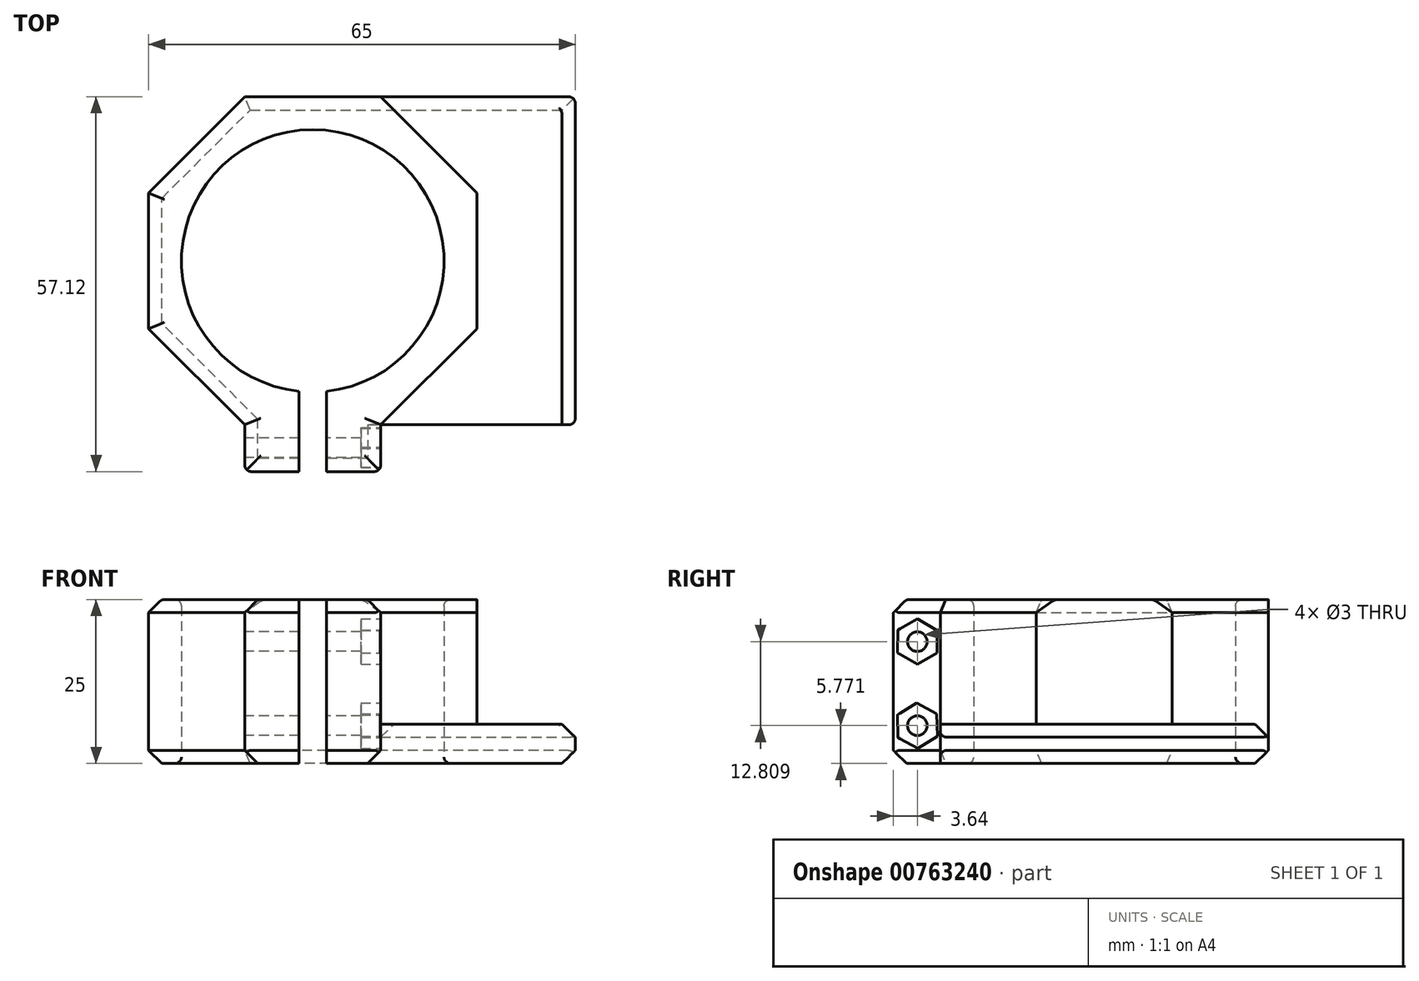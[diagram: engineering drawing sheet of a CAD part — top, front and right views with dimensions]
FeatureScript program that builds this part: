
annotation { "Feature Type Name" : "Feature", "Feature Type Description" : "" }
export const myFeature = defineFeature(function(context is Context, id is Id, definition is map)
    precondition{}
    {
        {
            var Q0;
            Q0=qCreatedBy(makeId("Top.planeOp"),FACE);
            var sketch = newSketch(context, id + "F0", { "sketchPlane" : qUnion([Q0])});
            skCircle(sketch, "E0", {"center": v(0, 0) * mm, "radius": 20 * mm});
            skCircle(sketch, "E1.cCircle", {"center": v(0, 0) * mm, "radius": 25 * mm, "construction": true});
            skLineSegment(sketch, "E1.0", {"start": v(-10.36, 25) * mm, "end": v(10.36, 25) * mm});
            skLineSegment(sketch, "E1.1", {"start": v(10.36, 25) * mm, "end": v(25, 10.36) * mm});
            skLineSegment(sketch, "E1.2", {"start": v(25, 10.36) * mm, "end": v(25, -10.36) * mm});
            skLineSegment(sketch, "E1.3", {"start": v(25, -10.36) * mm, "end": v(10.36, -25) * mm});
            skLineSegment(sketch, "E1.4", {"start": v(10.36, -25) * mm, "end": v(-10.36, -25) * mm});
            skLineSegment(sketch, "E1.5", {"start": v(-10.36, -25) * mm, "end": v(-25, -10.36) * mm});
            skLineSegment(sketch, "E1.6", {"start": v(-25, -10.36) * mm, "end": v(-25, 10.36) * mm});
            skLineSegment(sketch, "E1.7", {"start": v(-25, 10.36) * mm, "end": v(-10.36, 25) * mm});
            skPoint(sketch, "E1.0.midPoint", {"position": v(0, 25) * mm});
            skLineSegment(sketch, "E2.bottom", {"start": v(-10.36, 25) * mm, "end": v(40, 25) * mm});
            skLineSegment(sketch, "E2.top", {"start": v(-10.36, -25) * mm, "end": v(40, -25) * mm});
            skLineSegment(sketch, "E2.right", {"start": v(40, 25) * mm, "end": v(40, -25) * mm});
            skLineSegment(sketch, "E3.top", {"start": v(40, 25) * mm, "end": v(22.02, 25) * mm});
            skLineSegment(sketch, "E4", {"start": v(25, 10.36) * mm, "end": v(25, 25) * mm});
            skLineSegment(sketch, "E5", {"start": v(25, 25) * mm, "end": v(25, -10.36) * mm});
            skLineSegment(sketch, "E6", {"start": v(25, -10.36) * mm, "end": v(25, -25) * mm});
            skLineSegment(sketch, "E7.bottom", {"start": v(-10.36, -25) * mm, "end": v(10.36, -25) * mm});
            skLineSegment(sketch, "E7.top", {"start": v(-10.36, -32.12) * mm, "end": v(10.36, -32.12) * mm});
            skLineSegment(sketch, "E7.left", {"start": v(-10.36, -25) * mm, "end": v(-10.36, -32.12) * mm});
            skLineSegment(sketch, "E7.right", {"start": v(10.36, -25) * mm, "end": v(10.36, -32.12) * mm});
            skLineSegment(sketch, "E8.bottom", {"start": v(2.07, -32.12) * mm, "end": v(-2.07, -32.12) * mm});
            skLineSegment(sketch, "E8.top", {"start": v(2.07, -32.12) * mm, "end": v(-2.07, -32.12) * mm});
            skLineSegment(sketch, "E8.left", {"start": v(2.07, -32.12) * mm, "end": v(2.07, -32.12) * mm});
            skLineSegment(sketch, "E8.right", {"start": v(-2.07, -32.12) * mm, "end": v(-2.07, -32.12) * mm});
            skLineSegment(sketch, "E9.bottom", {"start": v(-2.07, -32.12) * mm, "end": v(2.07, -32.12) * mm});
            skLineSegment(sketch, "E9.top", {"start": v(-2.07, -19.9) * mm, "end": v(2.07, -19.9) * mm});
            skLineSegment(sketch, "E9.left", {"start": v(-2.07, -32.12) * mm, "end": v(-2.07, -19.9) * mm});
            skLineSegment(sketch, "E9.right", {"start": v(2.07, -32.12) * mm, "end": v(2.07, -19.9) * mm});
            skSolve(sketch);
        }
        {
            var Q0;
            {var subQ5=sQuery(id+"F0.wireOp",EDGE,"E1.1");Q0=makeQuery(id+"F0.imprint","IMPRINT",FACE,{"disambiguationData":[TD([[makeQuery(id+"F0.imprint","IMPRINT",EDGE,{"derivedFrom":subQ5}),-1.0]])]});}
            var Q1;
            {var subQ0=sQuery(id+"F0.wireOp",EDGE,"E7.left");Q1=makeQuery(id+"F0.imprint","IMPRINT",FACE,{"disambiguationData":[TD([[makeQuery(id+"F0.imprint","IMPRINT",EDGE,{"derivedFrom":subQ0}),1.0]])]});}
            var Q2;
            {var subQ0=sQuery(id+"F0.wireOp",EDGE,"E7.right");Q2=makeQuery(id+"F0.imprint","IMPRINT",FACE,{"disambiguationData":[TD([[makeQuery(id+"F0.imprint","IMPRINT",EDGE,{"derivedFrom":subQ0}),-1.0]])]});}
            extrude(context, id + "F1", {"entities" : qUnion([Q0, Q1, Q2]), "depth" : 25 * mm, "offsetDistance" : 25 * mm});
        }
        {
            var Q0;
            {var subQ1=sQuery(id+"F0.wireOp",EDGE,"E2.right");Q0=makeQuery(id+"F0.imprint","IMPRINT",FACE,{"disambiguationData":[TD([[makeQuery(id+"F0.imprint","IMPRINT",EDGE,{"derivedFrom":subQ1}),-1.0]])]});}
            var Q1;
            {var subQ0=sQuery(id+"F0.wireOp",EDGE,"E1.3");Q1=makeQuery(id+"F0.imprint","IMPRINT",FACE,{"disambiguationData":[TD([[makeQuery(id+"F0.imprint","IMPRINT",EDGE,{"derivedFrom":subQ0}),1.0]])]});}
            var Q2;
            {var subQ0=sQuery(id+"F0.wireOp",EDGE,"E1.1");Q2=makeQuery(id+"F0.imprint","IMPRINT",FACE,{"disambiguationData":[TD([[makeQuery(id+"F0.imprint","IMPRINT",EDGE,{"derivedFrom":subQ0}),1.0]])]});}
            extrude(context, id + "F2", {"entities" : qUnion([Q0, Q1, Q2]), "operationType" : NewBodyOperationType.ADD, "depth" : 6 * mm, "offsetDistance" : 25 * mm});
        }
        {
            var Q0;
            Q0=makeQuery(id+"F1.opExtrude","SWEPT_FACE",FACE,{"disambiguationData":[OSD([sQuery(id+"F0.wireOp",EDGE,"E7.left")])]});
            var sketch = newSketch(context, id + "F3", { "sketchPlane" : qUnion([Q0])});
            skCircle(sketch, "E10", {"center": v(28.48, 5.77) * mm, "radius": 1.5 * mm});
            skCircle(sketch, "E11", {"center": v(28.48, 18.58) * mm, "radius": 1.5 * mm});
            skSolve(sketch);
        }
        {
            var Q0;
            Q0=makeQuery(id+"F3.imprint","IMPRINT",FACE,{"disambiguationData":[TD([[makeQuery(id+"F3.imprint","IMPRINT",EDGE,{"derivedFrom":sQuery(id+"F3.wireOp",EDGE,"E11")}),1.0]])]});
            var Q1;
            Q1=makeQuery(id+"F3.imprint","IMPRINT",FACE,{"disambiguationData":[TD([[makeQuery(id+"F3.imprint","IMPRINT",EDGE,{"derivedFrom":sQuery(id+"F3.wireOp",EDGE,"E10")}),1.0]])]});
            extrude(context, id + "F4", {"entities" : qUnion([Q0, Q1]), "operationType" : NewBodyOperationType.REMOVE, "endBound" : BoundingType.THROUGH_ALL, "oppositeDirection" : true, "depth" : 25 * mm, "offsetDistance" : 25 * mm});
        }
        {
            var Q0;
            Q0=makeQuery(id+"F1.opExtrude","SWEPT_FACE",FACE,{"disambiguationData":[OSD([sQuery(id+"F0.wireOp",EDGE,"E7.right")])]});
            var sketch = newSketch(context, id + "F5", { "sketchPlane" : qUnion([Q0])});
            skCircle(sketch, "E12.cCircle", {"center": v(-28.48, 18.58) * mm, "radius": 3 * mm, "construction": true});
            skLineSegment(sketch, "E12.0", {"start": v(-28.5, 15.12) * mm, "end": v(-31.49, 16.86) * mm});
            skLineSegment(sketch, "E12.1", {"start": v(-31.49, 16.86) * mm, "end": v(-31.47, 20.32) * mm});
            skLineSegment(sketch, "E12.2", {"start": v(-31.47, 20.32) * mm, "end": v(-28.47, 22.04) * mm});
            skLineSegment(sketch, "E12.3", {"start": v(-28.47, 22.04) * mm, "end": v(-25.47, 20.3) * mm});
            skLineSegment(sketch, "E12.4", {"start": v(-25.47, 20.3) * mm, "end": v(-25.49, 16.84) * mm});
            skLineSegment(sketch, "E12.5", {"start": v(-25.49, 16.84) * mm, "end": v(-28.5, 15.12) * mm});
            skPoint(sketch, "E12.0.midPoint", {"position": v(-29.99, 15.99) * mm});
            skCircle(sketch, "E13.cCircle", {"center": v(-28.48, 5.77) * mm, "radius": 3 * mm, "construction": true});
            skLineSegment(sketch, "E13.0", {"start": v(-28.59, 9.23) * mm, "end": v(-25.54, 7.6) * mm});
            skLineSegment(sketch, "E13.1", {"start": v(-25.54, 7.6) * mm, "end": v(-25.43, 4.13) * mm});
            skLineSegment(sketch, "E13.2", {"start": v(-25.43, 4.13) * mm, "end": v(-28.37, 2.3) * mm});
            skLineSegment(sketch, "E13.3", {"start": v(-28.37, 2.3) * mm, "end": v(-31.42, 3.95) * mm});
            skLineSegment(sketch, "E13.4", {"start": v(-31.42, 3.95) * mm, "end": v(-31.53, 7.4) * mm});
            skLineSegment(sketch, "E13.5", {"start": v(-31.53, 7.4) * mm, "end": v(-28.59, 9.23) * mm});
            skPoint(sketch, "E13.0.midPoint", {"position": v(-27.06, 8.41) * mm});
            skSolve(sketch);
        }
        {
            var Q0;
            Q0=makeQuery(id+"F5.imprint","IMPRINT",FACE,{"disambiguationData":[TD([[makeQuery(id+"F5.imprint","IMPRINT",EDGE,{"derivedFrom":sQuery(id+"F5.wireOp",EDGE,"E12.0")}),-1.0]])]});
            var Q1;
            Q1=makeQuery(id+"F5.imprint","IMPRINT",FACE,{"disambiguationData":[TD([[makeQuery(id+"F5.imprint","IMPRINT",EDGE,{"derivedFrom":sQuery(id+"F5.wireOp",EDGE,"E13.0")}),-1.0]])]});
            extrude(context, id + "F6", {"entities" : qUnion([Q0, Q1]), "operationType" : NewBodyOperationType.REMOVE, "oppositeDirection" : true, "depth" : 3 * mm, "offsetDistance" : 25 * mm});
        }
        {
            var Q0;
            Q0=makeQuery(id+"F1.opExtrude","CAP_EDGE",EDGE,{"disambiguationData":[OSD([sQuery(id+"F0.wireOp",EDGE,"E1.5")])],"isStart":false});
            var Q1;
            Q1=makeQuery(id+"F1.opExtrude","CAP_EDGE",EDGE,{"disambiguationData":[OSD([sQuery(id+"F0.wireOp",EDGE,"E1.6")])],"isStart":false});
            var Q2;
            Q2=makeQuery(id+"F1.opExtrude","CAP_EDGE",EDGE,{"disambiguationData":[OSD([sQuery(id+"F0.wireOp",EDGE,"E1.7")])],"isStart":false});
            var Q3;
            Q3=makeQuery(id+"F1.opExtrude","CAP_EDGE",EDGE,{"disambiguationData":[OSD([sQuery(id+"F0.wireOp",EDGE,"E2.bottom")])],"isStart":false});
            var Q4;
            Q4=makeQuery(id+"F1.opExtrude","CAP_EDGE",EDGE,{"disambiguationData":[OSD([sQuery(id+"F0.wireOp",EDGE,"E1.1")])],"isStart":false});
            var Q5;
            Q5=makeQuery(id+"F1.opExtrude","CAP_EDGE",EDGE,{"disambiguationData":[OSD([sQuery(id+"F0.wireOp",EDGE,"E5")])],"isStart":false});
            var Q6;
            Q6=makeQuery(id+"F1.opExtrude","CAP_EDGE",EDGE,{"disambiguationData":[OSD([sQuery(id+"F0.wireOp",EDGE,"E1.3")])],"isStart":false});
            var Q7;
            Q7=makeQuery(id+"F1.opExtrude","CAP_EDGE",EDGE,{"disambiguationData":[OSD([sQuery(id+"F0.wireOp",EDGE,"E7.left")])],"isStart":false});
            var Q8;
            {var subQ0=sQuery(id+"F0.wireOp",EDGE,"E7.top");Q8=makeQuery(id+"F1.opExtrude","CAP_EDGE",EDGE,{"disambiguationData":[OSD([subQ0]),TDD([makeQuery(id+"F0.imprint","IMPRINT",EDGE,{"disambiguationData":[TD([[makeQuery(id+"F0.imprint","INTERSECT",VERTEX,{"derivedFrom":[subQ0,sQuery(id+"F0.wireOp",EDGE,"E7.left")]}),-1.0]])],"derivedFrom":subQ0})])],"isStart":false});}
            var Q9;
            {var subQ0=sQuery(id+"F0.wireOp",EDGE,"E7.top");Q9=makeQuery(id+"F1.opExtrude","CAP_EDGE",EDGE,{"disambiguationData":[OSD([subQ0]),TDD([makeQuery(id+"F0.imprint","IMPRINT",EDGE,{"disambiguationData":[TD([[makeQuery(id+"F0.imprint","INTERSECT",VERTEX,{"derivedFrom":[subQ0,sQuery(id+"F0.wireOp",EDGE,"E7.right")]}),1.0]])],"derivedFrom":subQ0})])],"isStart":false});}
            var Q10;
            Q10=makeQuery(id+"F1.opExtrude","CAP_EDGE",EDGE,{"disambiguationData":[OSD([sQuery(id+"F0.wireOp",EDGE,"E7.right")])],"isStart":false});
            var Q11;
            Q11=makeQuery(id+"F2.opExtrude","CAP_EDGE",EDGE,{"disambiguationData":[OSD([sQuery(id+"F0.wireOp",EDGE,"E1.3")])],"isStart":false});
            var Q12;
            Q12=makeQuery(id+"F2.opExtrude","CAP_EDGE",EDGE,{"disambiguationData":[OSD([sQuery(id+"F0.wireOp",EDGE,"E5")])],"isStart":false});
            var Q13;
            Q13=makeQuery(id+"F2.opExtrude","CAP_EDGE",EDGE,{"disambiguationData":[OSD([sQuery(id+"F0.wireOp",EDGE,"E1.1")])],"isStart":false});
            var Q14;
            {var subQ0=sQuery(id+"F0.wireOp",EDGE,"E7.top");Q14=makeQuery(id+"F1.opExtrude","CAP_EDGE",EDGE,{"disambiguationData":[OSD([subQ0]),TDD([makeQuery(id+"F0.imprint","IMPRINT",EDGE,{"disambiguationData":[TD([[makeQuery(id+"F0.imprint","INTERSECT",VERTEX,{"derivedFrom":[subQ0,sQuery(id+"F0.wireOp",EDGE,"E7.left")]}),-1.0]])],"derivedFrom":subQ0})])],"isStart":true});}
            var Q15;
            {var subQ0=sQuery(id+"F0.wireOp",EDGE,"E7.top");Q15=makeQuery(id+"F1.opExtrude","CAP_EDGE",EDGE,{"disambiguationData":[OSD([subQ0]),TDD([makeQuery(id+"F0.imprint","IMPRINT",EDGE,{"disambiguationData":[TD([[makeQuery(id+"F0.imprint","INTERSECT",VERTEX,{"derivedFrom":[subQ0,sQuery(id+"F0.wireOp",EDGE,"E7.right")]}),1.0]])],"derivedFrom":subQ0})])],"isStart":true});}
            var Q16;
            Q16=makeQuery(id+"F1.opExtrude","CAP_EDGE",EDGE,{"disambiguationData":[OSD([sQuery(id+"F0.wireOp",EDGE,"E7.left")])],"isStart":true});
            var Q17;
            Q17=makeQuery(id+"F1.opExtrude","CAP_EDGE",EDGE,{"disambiguationData":[OSD([sQuery(id+"F0.wireOp",EDGE,"E1.5")])],"isStart":true});
            var Q18;
            Q18=makeQuery(id+"F1.opExtrude","CAP_EDGE",EDGE,{"disambiguationData":[OSD([sQuery(id+"F0.wireOp",EDGE,"E1.6")])],"isStart":true});
            var Q19;
            Q19=makeQuery(id+"F1.opExtrude","CAP_EDGE",EDGE,{"disambiguationData":[OSD([sQuery(id+"F0.wireOp",EDGE,"E1.7")])],"isStart":true});
            var Q20;
            Q20=makeQuery(id+"F1.opExtrude","CAP_EDGE",EDGE,{"disambiguationData":[OSD([sQuery(id+"F0.wireOp",EDGE,"E7.right")])],"isStart":true});
            var Q21;
            {var subQ0=sQuery(id+"F0.wireOp",EDGE,"E2.bottom");Q21=makeQuery(id+"F2.boolean.opBoolean","MERGE",EDGE,{"derivedFrom":[makeQuery(id+"F1.opExtrude","CAP_EDGE",EDGE,{"disambiguationData":[OSD([subQ0])],"isStart":true}),makeQuery(id+"F2.opExtrude","CAP_EDGE",EDGE,{"disambiguationData":[OSD([subQ0,sQuery(id+"F0.wireOp",EDGE,"E3.top")])],"isStart":true})]});}
            var Q22;
            Q22=makeQuery(id+"F2.opExtrude","CAP_EDGE",EDGE,{"disambiguationData":[OSD([sQuery(id+"F0.wireOp",EDGE,"E2.bottom"),sQuery(id+"F0.wireOp",EDGE,"E3.top")])],"isStart":false});
            var Q23;
            Q23=makeQuery(id+"F2.opExtrude","CAP_EDGE",EDGE,{"disambiguationData":[OSD([sQuery(id+"F0.wireOp",EDGE,"E2.top")])],"isStart":true});
            var Q24;
            Q24=makeQuery(id+"F2.opExtrude","CAP_EDGE",EDGE,{"disambiguationData":[OSD([sQuery(id+"F0.wireOp",EDGE,"E2.right")])],"isStart":false});
            var Q25;
            Q25=makeQuery(id+"F2.opExtrude","CAP_EDGE",EDGE,{"disambiguationData":[OSD([sQuery(id+"F0.wireOp",EDGE,"E2.right")])],"isStart":true});
            chamfer(context, id + "F7", {"entities" : qUnion([Q0, Q1, Q2, Q3, Q4, Q5, Q6, Q7, Q8, Q9, Q10, Q11, Q12, Q13, Q14, Q15, Q16, Q17, Q18, Q19, Q20, Q21, Q22, Q23, Q24, Q25]), "width" : 2 * mm, "tangentPropagation" : true});
        }
        {
            var Q0;
            Q0=makeQuery(id+"F1.opExtrude","SWEPT_EDGE",EDGE,{"disambiguationData":[OSD([sQuery(id+"F0.wireOp",EDGE,"E7.top"),sQuery(id+"F0.wireOp",EDGE,"E7.right")])]});
            var Q1;
            Q1=makeQuery(id+"F1.opExtrude","SWEPT_EDGE",EDGE,{"disambiguationData":[OSD([sQuery(id+"F0.wireOp",EDGE,"E7.top"),sQuery(id+"F0.wireOp",EDGE,"E7.left")])]});
            var Q2;
            Q2=makeQuery(id+"F2.opExtrude","SWEPT_EDGE",EDGE,{"disambiguationData":[OSD([sQuery(id+"F0.wireOp",EDGE,"E2.right"),sQuery(id+"F0.wireOp",EDGE,"E2.top")])]});
            var Q3;
            Q3=makeQuery(id+"F2.opExtrude","SWEPT_EDGE",EDGE,{"disambiguationData":[OSD([sQuery(id+"F0.wireOp",EDGE,"E2.right"),sQuery(id+"F0.wireOp",EDGE,"E3.top")])]});
            var Q4;
            Q4=makeQuery(id+"F7.opChamfer","BLEND_EDGE",EDGE,{"blendedFrom":[makeQuery(id+"F2.opExtrude","CAP_EDGE",EDGE,{"disambiguationData":[OSD([sQuery(id+"F0.wireOp",EDGE,"E2.bottom"),sQuery(id+"F0.wireOp",EDGE,"E3.top")])],"isStart":false}),makeQuery(id+"F2.opExtrude","CAP_EDGE",EDGE,{"disambiguationData":[OSD([sQuery(id+"F0.wireOp",EDGE,"E2.right")])],"isStart":false})],"blendedInto":[]});
            var Q5;
            Q5=makeQuery(id+"F7.opChamfer","BLEND_EDGE",EDGE,{"blendedFrom":[makeQuery(id+"F2.opExtrude","CAP_EDGE",EDGE,{"disambiguationData":[OSD([sQuery(id+"F0.wireOp",EDGE,"E2.right")])],"isStart":false}),makeQuery(id+"F2.opExtrude","SWEPT_FACE",FACE,{"disambiguationData":[OSD([sQuery(id+"F0.wireOp",EDGE,"E2.top")])]})],"blendedInto":[makeQuery(id+"F2.opExtrude","SWEPT_FACE",FACE,{"disambiguationData":[OSD([sQuery(id+"F0.wireOp",EDGE,"E2.top")])]})]});
            var Q6;
            Q6=makeQuery(id+"F2.opExtrude","CAP_EDGE",EDGE,{"disambiguationData":[OSD([sQuery(id+"F0.wireOp",EDGE,"E2.top")])],"isStart":false});
            var Q7;
            {var subQ0=sQuery(id+"F0.wireOp",EDGE,"E3.top");var subQ1=sQuery(id+"F0.wireOp",EDGE,"E2.bottom");Q7=makeQuery(id+"F7.opChamfer","BLEND_EDGE",EDGE,{"blendedFrom":[makeQuery(id+"F2.opExtrude","CAP_EDGE",EDGE,{"disambiguationData":[OSD([subQ1,subQ0])],"isStart":false}),makeQuery(id+"F2.opExtrude","CAP_FACE",FACE,{"disambiguationData":[OSD([sQuery(id+"F0.wireOp",EDGE,"E1.1"),sQuery(id+"F0.wireOp",EDGE,"E1.3"),subQ1,sQuery(id+"F0.wireOp",EDGE,"E2.right"),sQuery(id+"F0.wireOp",EDGE,"E2.top"),subQ0,sQuery(id+"F0.wireOp",EDGE,"E5")])],"isStart":false})],"blendedInto":[makeQuery(id+"F2.opExtrude","CAP_FACE",FACE,{"disambiguationData":[OSD([sQuery(id+"F0.wireOp",EDGE,"E1.1"),sQuery(id+"F0.wireOp",EDGE,"E1.3"),subQ1,sQuery(id+"F0.wireOp",EDGE,"E2.right"),sQuery(id+"F0.wireOp",EDGE,"E2.top"),subQ0,sQuery(id+"F0.wireOp",EDGE,"E5")])],"isStart":false})]});}
            var Q8;
            Q8=makeQuery(id+"F1.opExtrude","CAP_EDGE",EDGE,{"disambiguationData":[OSD([sQuery(id+"F0.wireOp",EDGE,"E0")])],"isStart":false});
            var Q9;
            Q9=makeQuery(id+"F1.opExtrude","CAP_EDGE",EDGE,{"disambiguationData":[OSD([sQuery(id+"F0.wireOp",EDGE,"E0")])],"isStart":true});
            var Q10;
            {var subQ0=sQuery(id+"F0.wireOp",EDGE,"E1.5");Q10=makeQuery(id+"F7.opChamfer","BLEND_EDGE",EDGE,{"blendedFrom":[makeQuery(id+"F1.opExtrude","CAP_EDGE",EDGE,{"disambiguationData":[OSD([subQ0])],"isStart":false}),makeQuery(id+"F1.opExtrude","CAP_FACE",FACE,{"disambiguationData":[OSD([sQuery(id+"F0.wireOp",EDGE,"E0"),sQuery(id+"F0.wireOp",EDGE,"E1.1"),sQuery(id+"F0.wireOp",EDGE,"E1.3"),subQ0,sQuery(id+"F0.wireOp",EDGE,"E1.6"),sQuery(id+"F0.wireOp",EDGE,"E1.7"),sQuery(id+"F0.wireOp",EDGE,"E2.bottom"),sQuery(id+"F0.wireOp",EDGE,"E5"),sQuery(id+"F0.wireOp",EDGE,"E7.top"),sQuery(id+"F0.wireOp",EDGE,"E7.left"),sQuery(id+"F0.wireOp",EDGE,"E7.right"),sQuery(id+"F0.wireOp",EDGE,"E9.left"),sQuery(id+"F0.wireOp",EDGE,"E9.right")])],"isStart":false})],"blendedInto":[makeQuery(id+"F1.opExtrude","CAP_FACE",FACE,{"disambiguationData":[OSD([sQuery(id+"F0.wireOp",EDGE,"E0"),sQuery(id+"F0.wireOp",EDGE,"E1.1"),sQuery(id+"F0.wireOp",EDGE,"E1.3"),subQ0,sQuery(id+"F0.wireOp",EDGE,"E1.6"),sQuery(id+"F0.wireOp",EDGE,"E1.7"),sQuery(id+"F0.wireOp",EDGE,"E2.bottom"),sQuery(id+"F0.wireOp",EDGE,"E5"),sQuery(id+"F0.wireOp",EDGE,"E7.top"),sQuery(id+"F0.wireOp",EDGE,"E7.left"),sQuery(id+"F0.wireOp",EDGE,"E7.right"),sQuery(id+"F0.wireOp",EDGE,"E9.left"),sQuery(id+"F0.wireOp",EDGE,"E9.right")])],"isStart":false})]});}
            var Q11;
            {var subQ0=sQuery(id+"F0.wireOp",EDGE,"E1.6");Q11=makeQuery(id+"F7.opChamfer","BLEND_EDGE",EDGE,{"blendedFrom":[makeQuery(id+"F1.opExtrude","CAP_EDGE",EDGE,{"disambiguationData":[OSD([subQ0])],"isStart":false}),makeQuery(id+"F1.opExtrude","CAP_FACE",FACE,{"disambiguationData":[OSD([sQuery(id+"F0.wireOp",EDGE,"E0"),sQuery(id+"F0.wireOp",EDGE,"E1.1"),sQuery(id+"F0.wireOp",EDGE,"E1.3"),sQuery(id+"F0.wireOp",EDGE,"E1.5"),subQ0,sQuery(id+"F0.wireOp",EDGE,"E1.7"),sQuery(id+"F0.wireOp",EDGE,"E2.bottom"),sQuery(id+"F0.wireOp",EDGE,"E5"),sQuery(id+"F0.wireOp",EDGE,"E7.top"),sQuery(id+"F0.wireOp",EDGE,"E7.left"),sQuery(id+"F0.wireOp",EDGE,"E7.right"),sQuery(id+"F0.wireOp",EDGE,"E9.left"),sQuery(id+"F0.wireOp",EDGE,"E9.right")])],"isStart":false})],"blendedInto":[makeQuery(id+"F1.opExtrude","CAP_FACE",FACE,{"disambiguationData":[OSD([sQuery(id+"F0.wireOp",EDGE,"E0"),sQuery(id+"F0.wireOp",EDGE,"E1.1"),sQuery(id+"F0.wireOp",EDGE,"E1.3"),sQuery(id+"F0.wireOp",EDGE,"E1.5"),subQ0,sQuery(id+"F0.wireOp",EDGE,"E1.7"),sQuery(id+"F0.wireOp",EDGE,"E2.bottom"),sQuery(id+"F0.wireOp",EDGE,"E5"),sQuery(id+"F0.wireOp",EDGE,"E7.top"),sQuery(id+"F0.wireOp",EDGE,"E7.left"),sQuery(id+"F0.wireOp",EDGE,"E7.right"),sQuery(id+"F0.wireOp",EDGE,"E9.left"),sQuery(id+"F0.wireOp",EDGE,"E9.right")])],"isStart":false})]});}
            var Q12;
            {var subQ0=sQuery(id+"F0.wireOp",EDGE,"E1.7");Q12=makeQuery(id+"F7.opChamfer","BLEND_EDGE",EDGE,{"blendedFrom":[makeQuery(id+"F1.opExtrude","CAP_EDGE",EDGE,{"disambiguationData":[OSD([subQ0])],"isStart":false}),makeQuery(id+"F1.opExtrude","CAP_FACE",FACE,{"disambiguationData":[OSD([sQuery(id+"F0.wireOp",EDGE,"E0"),sQuery(id+"F0.wireOp",EDGE,"E1.1"),sQuery(id+"F0.wireOp",EDGE,"E1.3"),sQuery(id+"F0.wireOp",EDGE,"E1.5"),sQuery(id+"F0.wireOp",EDGE,"E1.6"),subQ0,sQuery(id+"F0.wireOp",EDGE,"E2.bottom"),sQuery(id+"F0.wireOp",EDGE,"E5"),sQuery(id+"F0.wireOp",EDGE,"E7.top"),sQuery(id+"F0.wireOp",EDGE,"E7.left"),sQuery(id+"F0.wireOp",EDGE,"E7.right"),sQuery(id+"F0.wireOp",EDGE,"E9.left"),sQuery(id+"F0.wireOp",EDGE,"E9.right")])],"isStart":false})],"blendedInto":[makeQuery(id+"F1.opExtrude","CAP_FACE",FACE,{"disambiguationData":[OSD([sQuery(id+"F0.wireOp",EDGE,"E0"),sQuery(id+"F0.wireOp",EDGE,"E1.1"),sQuery(id+"F0.wireOp",EDGE,"E1.3"),sQuery(id+"F0.wireOp",EDGE,"E1.5"),sQuery(id+"F0.wireOp",EDGE,"E1.6"),subQ0,sQuery(id+"F0.wireOp",EDGE,"E2.bottom"),sQuery(id+"F0.wireOp",EDGE,"E5"),sQuery(id+"F0.wireOp",EDGE,"E7.top"),sQuery(id+"F0.wireOp",EDGE,"E7.left"),sQuery(id+"F0.wireOp",EDGE,"E7.right"),sQuery(id+"F0.wireOp",EDGE,"E9.left"),sQuery(id+"F0.wireOp",EDGE,"E9.right")])],"isStart":false})]});}
            var Q13;
            {var subQ0=sQuery(id+"F0.wireOp",EDGE,"E2.bottom");Q13=makeQuery(id+"F7.opChamfer","BLEND_EDGE",EDGE,{"blendedFrom":[makeQuery(id+"F1.opExtrude","CAP_EDGE",EDGE,{"disambiguationData":[OSD([subQ0])],"isStart":false}),makeQuery(id+"F1.opExtrude","CAP_FACE",FACE,{"disambiguationData":[OSD([sQuery(id+"F0.wireOp",EDGE,"E0"),sQuery(id+"F0.wireOp",EDGE,"E1.1"),sQuery(id+"F0.wireOp",EDGE,"E1.3"),sQuery(id+"F0.wireOp",EDGE,"E1.5"),sQuery(id+"F0.wireOp",EDGE,"E1.6"),sQuery(id+"F0.wireOp",EDGE,"E1.7"),subQ0,sQuery(id+"F0.wireOp",EDGE,"E5"),sQuery(id+"F0.wireOp",EDGE,"E7.top"),sQuery(id+"F0.wireOp",EDGE,"E7.left"),sQuery(id+"F0.wireOp",EDGE,"E7.right"),sQuery(id+"F0.wireOp",EDGE,"E9.left"),sQuery(id+"F0.wireOp",EDGE,"E9.right")])],"isStart":false})],"blendedInto":[makeQuery(id+"F1.opExtrude","CAP_FACE",FACE,{"disambiguationData":[OSD([sQuery(id+"F0.wireOp",EDGE,"E0"),sQuery(id+"F0.wireOp",EDGE,"E1.1"),sQuery(id+"F0.wireOp",EDGE,"E1.3"),sQuery(id+"F0.wireOp",EDGE,"E1.5"),sQuery(id+"F0.wireOp",EDGE,"E1.6"),sQuery(id+"F0.wireOp",EDGE,"E1.7"),subQ0,sQuery(id+"F0.wireOp",EDGE,"E5"),sQuery(id+"F0.wireOp",EDGE,"E7.top"),sQuery(id+"F0.wireOp",EDGE,"E7.left"),sQuery(id+"F0.wireOp",EDGE,"E7.right"),sQuery(id+"F0.wireOp",EDGE,"E9.left"),sQuery(id+"F0.wireOp",EDGE,"E9.right")])],"isStart":false})]});}
            var Q14;
            {var subQ0=sQuery(id+"F0.wireOp",EDGE,"E1.3");Q14=makeQuery(id+"F7.opChamfer","BLEND_EDGE",EDGE,{"blendedFrom":[makeQuery(id+"F1.opExtrude","CAP_EDGE",EDGE,{"disambiguationData":[OSD([subQ0])],"isStart":false}),makeQuery(id+"F1.opExtrude","CAP_FACE",FACE,{"disambiguationData":[OSD([sQuery(id+"F0.wireOp",EDGE,"E0"),sQuery(id+"F0.wireOp",EDGE,"E1.1"),subQ0,sQuery(id+"F0.wireOp",EDGE,"E1.5"),sQuery(id+"F0.wireOp",EDGE,"E1.6"),sQuery(id+"F0.wireOp",EDGE,"E1.7"),sQuery(id+"F0.wireOp",EDGE,"E2.bottom"),sQuery(id+"F0.wireOp",EDGE,"E5"),sQuery(id+"F0.wireOp",EDGE,"E7.top"),sQuery(id+"F0.wireOp",EDGE,"E7.left"),sQuery(id+"F0.wireOp",EDGE,"E7.right"),sQuery(id+"F0.wireOp",EDGE,"E9.left"),sQuery(id+"F0.wireOp",EDGE,"E9.right")])],"isStart":false})],"blendedInto":[makeQuery(id+"F1.opExtrude","CAP_FACE",FACE,{"disambiguationData":[OSD([sQuery(id+"F0.wireOp",EDGE,"E0"),sQuery(id+"F0.wireOp",EDGE,"E1.1"),subQ0,sQuery(id+"F0.wireOp",EDGE,"E1.5"),sQuery(id+"F0.wireOp",EDGE,"E1.6"),sQuery(id+"F0.wireOp",EDGE,"E1.7"),sQuery(id+"F0.wireOp",EDGE,"E2.bottom"),sQuery(id+"F0.wireOp",EDGE,"E5"),sQuery(id+"F0.wireOp",EDGE,"E7.top"),sQuery(id+"F0.wireOp",EDGE,"E7.left"),sQuery(id+"F0.wireOp",EDGE,"E7.right"),sQuery(id+"F0.wireOp",EDGE,"E9.left"),sQuery(id+"F0.wireOp",EDGE,"E9.right")])],"isStart":false})]});}
            var Q15;
            {var subQ0=sQuery(id+"F0.wireOp",EDGE,"E5");Q15=makeQuery(id+"F7.opChamfer","BLEND_EDGE",EDGE,{"blendedFrom":[makeQuery(id+"F1.opExtrude","CAP_EDGE",EDGE,{"disambiguationData":[OSD([subQ0])],"isStart":false}),makeQuery(id+"F1.opExtrude","CAP_FACE",FACE,{"disambiguationData":[OSD([sQuery(id+"F0.wireOp",EDGE,"E0"),sQuery(id+"F0.wireOp",EDGE,"E1.1"),sQuery(id+"F0.wireOp",EDGE,"E1.3"),sQuery(id+"F0.wireOp",EDGE,"E1.5"),sQuery(id+"F0.wireOp",EDGE,"E1.6"),sQuery(id+"F0.wireOp",EDGE,"E1.7"),sQuery(id+"F0.wireOp",EDGE,"E2.bottom"),subQ0,sQuery(id+"F0.wireOp",EDGE,"E7.top"),sQuery(id+"F0.wireOp",EDGE,"E7.left"),sQuery(id+"F0.wireOp",EDGE,"E7.right"),sQuery(id+"F0.wireOp",EDGE,"E9.left"),sQuery(id+"F0.wireOp",EDGE,"E9.right")])],"isStart":false})],"blendedInto":[makeQuery(id+"F1.opExtrude","CAP_FACE",FACE,{"disambiguationData":[OSD([sQuery(id+"F0.wireOp",EDGE,"E0"),sQuery(id+"F0.wireOp",EDGE,"E1.1"),sQuery(id+"F0.wireOp",EDGE,"E1.3"),sQuery(id+"F0.wireOp",EDGE,"E1.5"),sQuery(id+"F0.wireOp",EDGE,"E1.6"),sQuery(id+"F0.wireOp",EDGE,"E1.7"),sQuery(id+"F0.wireOp",EDGE,"E2.bottom"),subQ0,sQuery(id+"F0.wireOp",EDGE,"E7.top"),sQuery(id+"F0.wireOp",EDGE,"E7.left"),sQuery(id+"F0.wireOp",EDGE,"E7.right"),sQuery(id+"F0.wireOp",EDGE,"E9.left"),sQuery(id+"F0.wireOp",EDGE,"E9.right")])],"isStart":false})]});}
            var Q16;
            {var subQ0=sQuery(id+"F0.wireOp",EDGE,"E1.1");Q16=makeQuery(id+"F7.opChamfer","BLEND_EDGE",EDGE,{"blendedFrom":[makeQuery(id+"F1.opExtrude","CAP_EDGE",EDGE,{"disambiguationData":[OSD([subQ0])],"isStart":false}),makeQuery(id+"F1.opExtrude","CAP_FACE",FACE,{"disambiguationData":[OSD([sQuery(id+"F0.wireOp",EDGE,"E0"),subQ0,sQuery(id+"F0.wireOp",EDGE,"E1.3"),sQuery(id+"F0.wireOp",EDGE,"E1.5"),sQuery(id+"F0.wireOp",EDGE,"E1.6"),sQuery(id+"F0.wireOp",EDGE,"E1.7"),sQuery(id+"F0.wireOp",EDGE,"E2.bottom"),sQuery(id+"F0.wireOp",EDGE,"E5"),sQuery(id+"F0.wireOp",EDGE,"E7.top"),sQuery(id+"F0.wireOp",EDGE,"E7.left"),sQuery(id+"F0.wireOp",EDGE,"E7.right"),sQuery(id+"F0.wireOp",EDGE,"E9.left"),sQuery(id+"F0.wireOp",EDGE,"E9.right")])],"isStart":false})],"blendedInto":[makeQuery(id+"F1.opExtrude","CAP_FACE",FACE,{"disambiguationData":[OSD([sQuery(id+"F0.wireOp",EDGE,"E0"),subQ0,sQuery(id+"F0.wireOp",EDGE,"E1.3"),sQuery(id+"F0.wireOp",EDGE,"E1.5"),sQuery(id+"F0.wireOp",EDGE,"E1.6"),sQuery(id+"F0.wireOp",EDGE,"E1.7"),sQuery(id+"F0.wireOp",EDGE,"E2.bottom"),sQuery(id+"F0.wireOp",EDGE,"E5"),sQuery(id+"F0.wireOp",EDGE,"E7.top"),sQuery(id+"F0.wireOp",EDGE,"E7.left"),sQuery(id+"F0.wireOp",EDGE,"E7.right"),sQuery(id+"F0.wireOp",EDGE,"E9.left"),sQuery(id+"F0.wireOp",EDGE,"E9.right")])],"isStart":false})]});}
            var Q17;
            {var subQ0=sQuery(id+"F0.wireOp",EDGE,"E7.left");Q17=makeQuery(id+"F7.opChamfer","BLEND_EDGE",EDGE,{"blendedFrom":[makeQuery(id+"F1.opExtrude","CAP_EDGE",EDGE,{"disambiguationData":[OSD([subQ0])],"isStart":false}),makeQuery(id+"F1.opExtrude","CAP_FACE",FACE,{"disambiguationData":[OSD([sQuery(id+"F0.wireOp",EDGE,"E0"),sQuery(id+"F0.wireOp",EDGE,"E1.1"),sQuery(id+"F0.wireOp",EDGE,"E1.3"),sQuery(id+"F0.wireOp",EDGE,"E1.5"),sQuery(id+"F0.wireOp",EDGE,"E1.6"),sQuery(id+"F0.wireOp",EDGE,"E1.7"),sQuery(id+"F0.wireOp",EDGE,"E2.bottom"),sQuery(id+"F0.wireOp",EDGE,"E5"),sQuery(id+"F0.wireOp",EDGE,"E7.top"),subQ0,sQuery(id+"F0.wireOp",EDGE,"E7.right"),sQuery(id+"F0.wireOp",EDGE,"E9.left"),sQuery(id+"F0.wireOp",EDGE,"E9.right")])],"isStart":false})],"blendedInto":[makeQuery(id+"F1.opExtrude","CAP_FACE",FACE,{"disambiguationData":[OSD([sQuery(id+"F0.wireOp",EDGE,"E0"),sQuery(id+"F0.wireOp",EDGE,"E1.1"),sQuery(id+"F0.wireOp",EDGE,"E1.3"),sQuery(id+"F0.wireOp",EDGE,"E1.5"),sQuery(id+"F0.wireOp",EDGE,"E1.6"),sQuery(id+"F0.wireOp",EDGE,"E1.7"),sQuery(id+"F0.wireOp",EDGE,"E2.bottom"),sQuery(id+"F0.wireOp",EDGE,"E5"),sQuery(id+"F0.wireOp",EDGE,"E7.top"),subQ0,sQuery(id+"F0.wireOp",EDGE,"E7.right"),sQuery(id+"F0.wireOp",EDGE,"E9.left"),sQuery(id+"F0.wireOp",EDGE,"E9.right")])],"isStart":false})]});}
            var Q18;
            {var subQ0=sQuery(id+"F0.wireOp",EDGE,"E9.left");var subQ1=sQuery(id+"F0.wireOp",EDGE,"E7.left");var subQ2=sQuery(id+"F0.wireOp",EDGE,"E7.top");Q18=makeQuery(id+"F7.opChamfer","BLEND_EDGE",EDGE,{"blendedFrom":[makeQuery(id+"F1.opExtrude","CAP_EDGE",EDGE,{"disambiguationData":[OSD([subQ2]),TDD([makeQuery(id+"F0.imprint","IMPRINT",EDGE,{"disambiguationData":[TD([[makeQuery(id+"F0.imprint","INTERSECT",VERTEX,{"derivedFrom":[subQ2,subQ1]}),-1.0]])],"derivedFrom":subQ2})])],"isStart":false}),makeQuery(id+"F1.opExtrude","CAP_FACE",FACE,{"disambiguationData":[OSD([sQuery(id+"F0.wireOp",EDGE,"E0"),sQuery(id+"F0.wireOp",EDGE,"E1.1"),sQuery(id+"F0.wireOp",EDGE,"E1.3"),sQuery(id+"F0.wireOp",EDGE,"E1.5"),sQuery(id+"F0.wireOp",EDGE,"E1.6"),sQuery(id+"F0.wireOp",EDGE,"E1.7"),sQuery(id+"F0.wireOp",EDGE,"E2.bottom"),sQuery(id+"F0.wireOp",EDGE,"E5"),subQ2,subQ1,sQuery(id+"F0.wireOp",EDGE,"E7.right"),subQ0,sQuery(id+"F0.wireOp",EDGE,"E9.right")])],"isStart":false})],"blendedInto":[makeQuery(id+"F1.opExtrude","CAP_FACE",FACE,{"disambiguationData":[OSD([sQuery(id+"F0.wireOp",EDGE,"E0"),sQuery(id+"F0.wireOp",EDGE,"E1.1"),sQuery(id+"F0.wireOp",EDGE,"E1.3"),sQuery(id+"F0.wireOp",EDGE,"E1.5"),sQuery(id+"F0.wireOp",EDGE,"E1.6"),sQuery(id+"F0.wireOp",EDGE,"E1.7"),sQuery(id+"F0.wireOp",EDGE,"E2.bottom"),sQuery(id+"F0.wireOp",EDGE,"E5"),subQ2,subQ1,sQuery(id+"F0.wireOp",EDGE,"E7.right"),subQ0,sQuery(id+"F0.wireOp",EDGE,"E9.right")])],"isStart":false})]});}
            var Q19;
            {var subQ0=sQuery(id+"F0.wireOp",EDGE,"E9.right");var subQ1=sQuery(id+"F0.wireOp",EDGE,"E7.right");var subQ2=sQuery(id+"F0.wireOp",EDGE,"E7.top");Q19=makeQuery(id+"F7.opChamfer","BLEND_EDGE",EDGE,{"blendedFrom":[makeQuery(id+"F1.opExtrude","CAP_EDGE",EDGE,{"disambiguationData":[OSD([subQ2]),TDD([makeQuery(id+"F0.imprint","IMPRINT",EDGE,{"disambiguationData":[TD([[makeQuery(id+"F0.imprint","INTERSECT",VERTEX,{"derivedFrom":[subQ2,subQ1]}),1.0]])],"derivedFrom":subQ2})])],"isStart":false}),makeQuery(id+"F1.opExtrude","CAP_FACE",FACE,{"disambiguationData":[OSD([sQuery(id+"F0.wireOp",EDGE,"E0"),sQuery(id+"F0.wireOp",EDGE,"E1.1"),sQuery(id+"F0.wireOp",EDGE,"E1.3"),sQuery(id+"F0.wireOp",EDGE,"E1.5"),sQuery(id+"F0.wireOp",EDGE,"E1.6"),sQuery(id+"F0.wireOp",EDGE,"E1.7"),sQuery(id+"F0.wireOp",EDGE,"E2.bottom"),sQuery(id+"F0.wireOp",EDGE,"E5"),subQ2,sQuery(id+"F0.wireOp",EDGE,"E7.left"),subQ1,sQuery(id+"F0.wireOp",EDGE,"E9.left"),subQ0])],"isStart":false})],"blendedInto":[makeQuery(id+"F1.opExtrude","CAP_FACE",FACE,{"disambiguationData":[OSD([sQuery(id+"F0.wireOp",EDGE,"E0"),sQuery(id+"F0.wireOp",EDGE,"E1.1"),sQuery(id+"F0.wireOp",EDGE,"E1.3"),sQuery(id+"F0.wireOp",EDGE,"E1.5"),sQuery(id+"F0.wireOp",EDGE,"E1.6"),sQuery(id+"F0.wireOp",EDGE,"E1.7"),sQuery(id+"F0.wireOp",EDGE,"E2.bottom"),sQuery(id+"F0.wireOp",EDGE,"E5"),subQ2,sQuery(id+"F0.wireOp",EDGE,"E7.left"),subQ1,sQuery(id+"F0.wireOp",EDGE,"E9.left"),subQ0])],"isStart":false})]});}
            var Q20;
            {var subQ0=sQuery(id+"F0.wireOp",EDGE,"E7.right");Q20=makeQuery(id+"F7.opChamfer","BLEND_EDGE",EDGE,{"blendedFrom":[makeQuery(id+"F1.opExtrude","CAP_EDGE",EDGE,{"disambiguationData":[OSD([subQ0])],"isStart":false}),makeQuery(id+"F1.opExtrude","CAP_FACE",FACE,{"disambiguationData":[OSD([sQuery(id+"F0.wireOp",EDGE,"E0"),sQuery(id+"F0.wireOp",EDGE,"E1.1"),sQuery(id+"F0.wireOp",EDGE,"E1.3"),sQuery(id+"F0.wireOp",EDGE,"E1.5"),sQuery(id+"F0.wireOp",EDGE,"E1.6"),sQuery(id+"F0.wireOp",EDGE,"E1.7"),sQuery(id+"F0.wireOp",EDGE,"E2.bottom"),sQuery(id+"F0.wireOp",EDGE,"E5"),sQuery(id+"F0.wireOp",EDGE,"E7.top"),sQuery(id+"F0.wireOp",EDGE,"E7.left"),subQ0,sQuery(id+"F0.wireOp",EDGE,"E9.left"),sQuery(id+"F0.wireOp",EDGE,"E9.right")])],"isStart":false})],"blendedInto":[makeQuery(id+"F1.opExtrude","CAP_FACE",FACE,{"disambiguationData":[OSD([sQuery(id+"F0.wireOp",EDGE,"E0"),sQuery(id+"F0.wireOp",EDGE,"E1.1"),sQuery(id+"F0.wireOp",EDGE,"E1.3"),sQuery(id+"F0.wireOp",EDGE,"E1.5"),sQuery(id+"F0.wireOp",EDGE,"E1.6"),sQuery(id+"F0.wireOp",EDGE,"E1.7"),sQuery(id+"F0.wireOp",EDGE,"E2.bottom"),sQuery(id+"F0.wireOp",EDGE,"E5"),sQuery(id+"F0.wireOp",EDGE,"E7.top"),sQuery(id+"F0.wireOp",EDGE,"E7.left"),subQ0,sQuery(id+"F0.wireOp",EDGE,"E9.left"),sQuery(id+"F0.wireOp",EDGE,"E9.right")])],"isStart":false})]});}
            fillet(context, id + "F8", {"entities" : qUnion([Q0, Q1, Q2, Q3, Q4, Q5, Q6, Q7, Q8, Q9, Q10, Q11, Q12, Q13, Q14, Q15, Q16, Q17, Q18, Q19, Q20]), "radius" : 1 * mm, "tangentPropagation" : true, "allowEdgeOverflow" : false});
        }
    });
